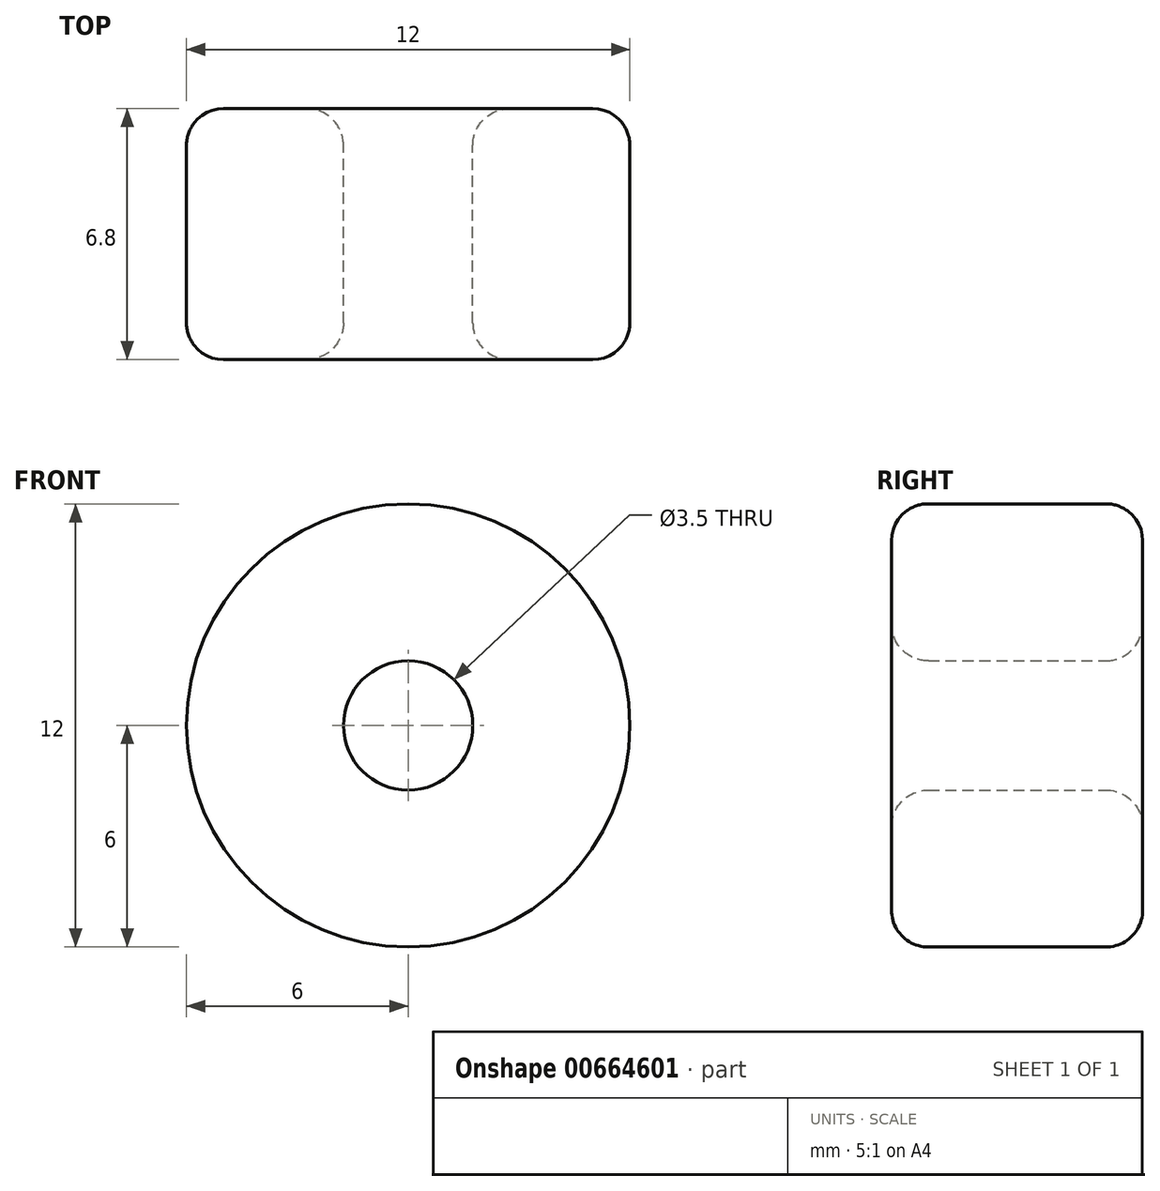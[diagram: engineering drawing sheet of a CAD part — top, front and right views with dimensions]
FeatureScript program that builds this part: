
annotation { "Feature Type Name" : "Feature", "Feature Type Description" : "" }
export const myFeature = defineFeature(function(context is Context, id is Id, definition is map)
    precondition{}
    {
        {
            var Q0;
            Q0=qCreatedBy(makeId("Front.planeOp"),FACE);
            var sketch = newSketch(context, id + "F0", { "sketchPlane" : qUnion([Q0])});
            skCircle(sketch, "E0", {"center": v(0, 0) * mm, "radius": 6 * mm});
            skCircle(sketch, "E1", {"center": v(0, 0) * mm, "radius": 1.75 * mm});
            skSolve(sketch);
        }
        {
            var Q0;
            Q0 = qSketchRegion(id + "F0", true);
            extrude(context, id + "F1", {"entities" : qUnion([Q0]), "depth" : 6.8 * mm, "offsetDistance" : 25.4 * mm});
        }
        {
            var Q0;
            Q0=makeQuery(id+"F1.opExtrude","CAP_EDGE",EDGE,{"disambiguationData":[OSD([sQuery(id+"F0.wireOp",EDGE,"E0")])],"isStart":false});
            var Q1;
            Q1=makeQuery(id+"F1.opExtrude","CAP_EDGE",EDGE,{"disambiguationData":[OSD([sQuery(id+"F0.wireOp",EDGE,"E0")])],"isStart":true});
            fillet(context, id + "F2", {"entities" : qUnion([Q0, Q1]), "radius" : 1 * mm, "tangentPropagation" : true, "allowEdgeOverflow" : false});
        }
        {
            var Q0;
            Q0=makeQuery(id+"F1.opExtrude","CAP_EDGE",EDGE,{"disambiguationData":[OSD([sQuery(id+"F0.wireOp",EDGE,"E1")])],"isStart":false});
            var Q1;
            Q1=makeQuery(id+"F1.opExtrude","CAP_EDGE",EDGE,{"disambiguationData":[OSD([sQuery(id+"F0.wireOp",EDGE,"E1")])],"isStart":true});
            fillet(context, id + "F3", {"entities" : qUnion([Q0, Q1]), "radius" : 1 * mm, "tangentPropagation" : true, "allowEdgeOverflow" : false});
        }
    });
